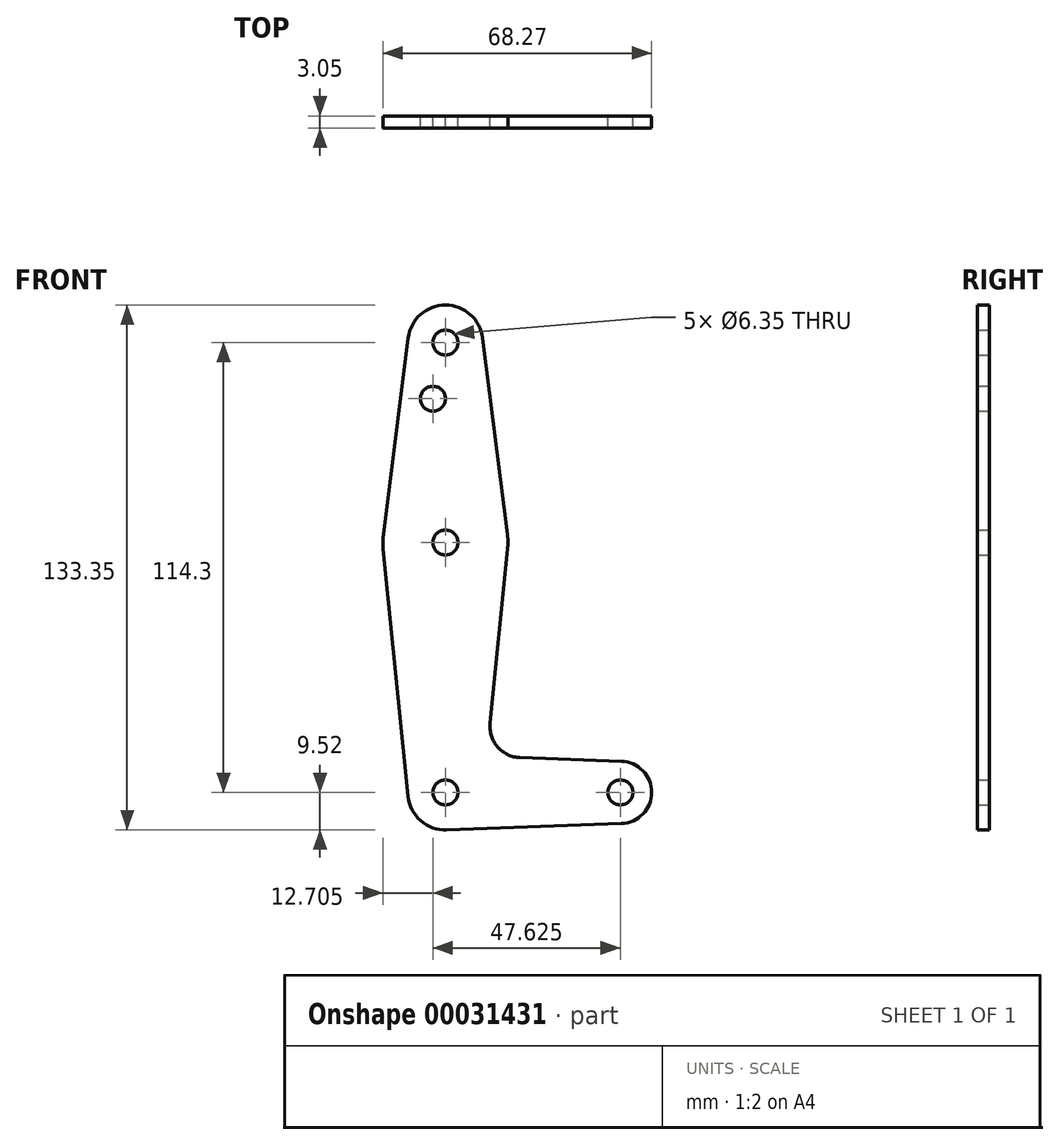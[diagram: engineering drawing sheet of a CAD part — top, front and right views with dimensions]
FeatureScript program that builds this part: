
annotation { "Feature Type Name" : "Feature", "Feature Type Description" : "" }
export const myFeature = defineFeature(function(context is Context, id is Id, definition is map)
    precondition{}
    {
        {
            var Q0;
            Q0=qCreatedBy(makeId("Front.planeOp"),FACE);
            var sketch = newSketch(context, id + "F0", { "sketchPlane" : qUnion([Q0])});
            skLineSegment(sketch, "E0", {"start": v(0, 114.3) * mm, "end": v(0, 0) * mm, "construction": true});
            skLineSegment(sketch, "E1", {"start": v(0, 0) * mm, "end": v(44.45, 0) * mm, "construction": true});
            skCircle(sketch, "E2", {"center": v(0, 114.3) * mm, "radius": 9.53 * mm});
            skCircle(sketch, "E3", {"center": v(0, 0) * mm, "radius": 9.53 * mm});
            skCircle(sketch, "E4", {"center": v(44.45, 0) * mm, "radius": 7.94 * mm});
            skCircle(sketch, "E5", {"center": v(0, 63.5) * mm, "radius": 15.88 * mm});
            skLineSegment(sketch, "E6", {"start": v(-9.45, 115.5) * mm, "end": v(-15.75, 65.48) * mm});
            skLineSegment(sketch, "E7", {"start": v(0.34, -9.52) * mm, "end": v(44.73, -7.93) * mm});
            skLineSegment(sketch, "E8", {"start": v(44.73, 7.93) * mm, "end": v(18.97, 8.85) * mm});
            skLineSegment(sketch, "E9", {"start": v(11.34, 17.6) * mm, "end": v(15.8, 61.91) * mm});
            skLineSegment(sketch, "E10", {"start": v(9.45, 115.5) * mm, "end": v(15.75, 65.48) * mm});
            skLineSegment(sketch, "E11", {"start": v(-15.8, 61.91) * mm, "end": v(-9.48, -0.95) * mm});
            skCircle(sketch, "E12", {"center": v(-3.17, 100.03) * mm, "radius": 3.18 * mm});
            skCircle(sketch, "E13", {"center": v(0, 114.3) * mm, "radius": 3.18 * mm});
            skCircle(sketch, "E14", {"center": v(0, 63.5) * mm, "radius": 3.18 * mm});
            skCircle(sketch, "E15", {"center": v(0, 0) * mm, "radius": 3.18 * mm});
            skCircle(sketch, "E16", {"center": v(44.45, 0) * mm, "radius": 3.18 * mm});
            skArc(sketch, "E17.filletArc", {"start": v(11.34, 17.6) * mm, "mid": v(13.26, 11.57) * mm, "end": v(18.97, 8.85) * mm});
            skSolve(sketch);
        }
        {
            var Q0;
            Q0 = qSketchRegion(id + "F0", true);
            extrude(context, id + "F1", {"entities" : qUnion([Q0]), "depth" : 3.05 * mm});
        }
    });
